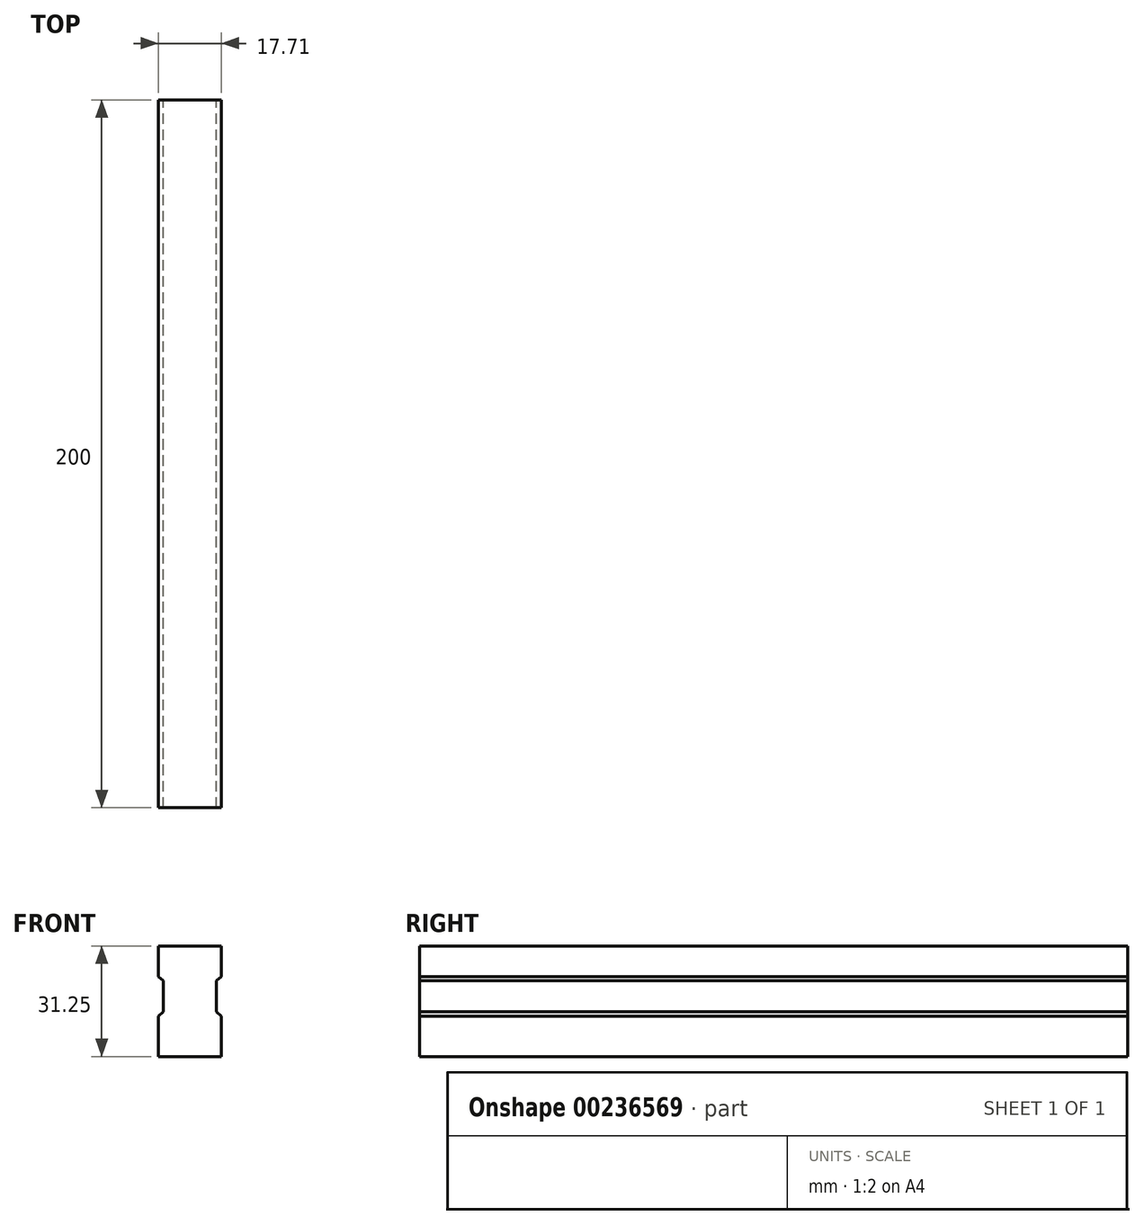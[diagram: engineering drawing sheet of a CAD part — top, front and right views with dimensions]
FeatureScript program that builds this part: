
annotation { "Feature Type Name" : "Feature", "Feature Type Description" : "" }
export const myFeature = defineFeature(function(context is Context, id is Id, definition is map)
    precondition{}
    {
        {
            var Q0;
            Q0=qCreatedBy(makeId("Front.planeOp"),FACE);
            var sketch = newSketch(context, id + "F0", { "sketchPlane" : qUnion([Q0])});
            skLineSegment(sketch, "E0.bottom", {"start": v(0, 0) * mm, "end": v(17.7, 0) * mm, "construction": true});
            skLineSegment(sketch, "E0.top", {"start": v(0, 31.25) * mm, "end": v(17.7, 31.25) * mm, "construction": true});
            skLineSegment(sketch, "E0.left", {"start": v(0, 0) * mm, "end": v(0, 31.25) * mm, "construction": true});
            skLineSegment(sketch, "E0.right", {"start": v(17.7, 0) * mm, "end": v(17.7, 31.25) * mm, "construction": true});
            skLineSegment(sketch, "E1", {"start": v(8.85, 31.25) * mm, "end": v(8.85, 0) * mm, "construction": true});
            skLineSegment(sketch, "E2", {"start": v(8.85, 0) * mm, "end": v(0, 0) * mm});
            skLineSegment(sketch, "E3", {"start": v(0, 11.35) * mm, "end": v(1.35, 12.6) * mm});
            skLineSegment(sketch, "E4", {"start": v(1.35, 12.6) * mm, "end": v(1.35, 21.35) * mm});
            skLineSegment(sketch, "E5", {"start": v(1.35, 21.35) * mm, "end": v(0, 22.6) * mm});
            skLineSegment(sketch, "E6", {"start": v(0, 22.6) * mm, "end": v(0, 31.25) * mm});
            skLineSegment(sketch, "E7", {"start": v(8.85, 31.25) * mm, "end": v(0, 31.25) * mm});
            skLineSegment(sketch, "E8", {"start": v(0, 0) * mm, "end": v(0, 11.35) * mm});
            skLineSegment(sketch, "E9.MirrorCS", {"start": v(16.35, 21.35) * mm, "end": v(17.7, 22.6) * mm});
            skLineSegment(sketch, "E10.MirrorCS", {"start": v(17.7, 11.35) * mm, "end": v(16.35, 12.6) * mm});
            skLineSegment(sketch, "E11.MirrorCS", {"start": v(17.7, 0) * mm, "end": v(17.7, 11.35) * mm});
            skLineSegment(sketch, "E12.MirrorCS", {"start": v(8.85, 31.25) * mm, "end": v(17.7, 31.25) * mm});
            skLineSegment(sketch, "E13.MirrorCS", {"start": v(8.85, 0) * mm, "end": v(17.7, 0) * mm});
            skLineSegment(sketch, "E14.MirrorCS", {"start": v(16.35, 12.6) * mm, "end": v(16.35, 21.35) * mm});
            skLineSegment(sketch, "E15.MirrorCS", {"start": v(17.7, 22.6) * mm, "end": v(17.7, 31.25) * mm});
            skSolve(sketch);
        }
        {
            var Q0;
            Q0=makeQuery(id+"F0.imprint","IMPRINT",FACE,{"disambiguationData":[TD([[makeQuery(id+"F0.imprint","IMPRINT",EDGE,{"derivedFrom":sQuery(id+"F0.wireOp",EDGE,"E2")}),-1.0]])]});
            extrude(context, id + "F1", {"entities" : qUnion([Q0]), "depth" : 200 * mm});
        }
    });
